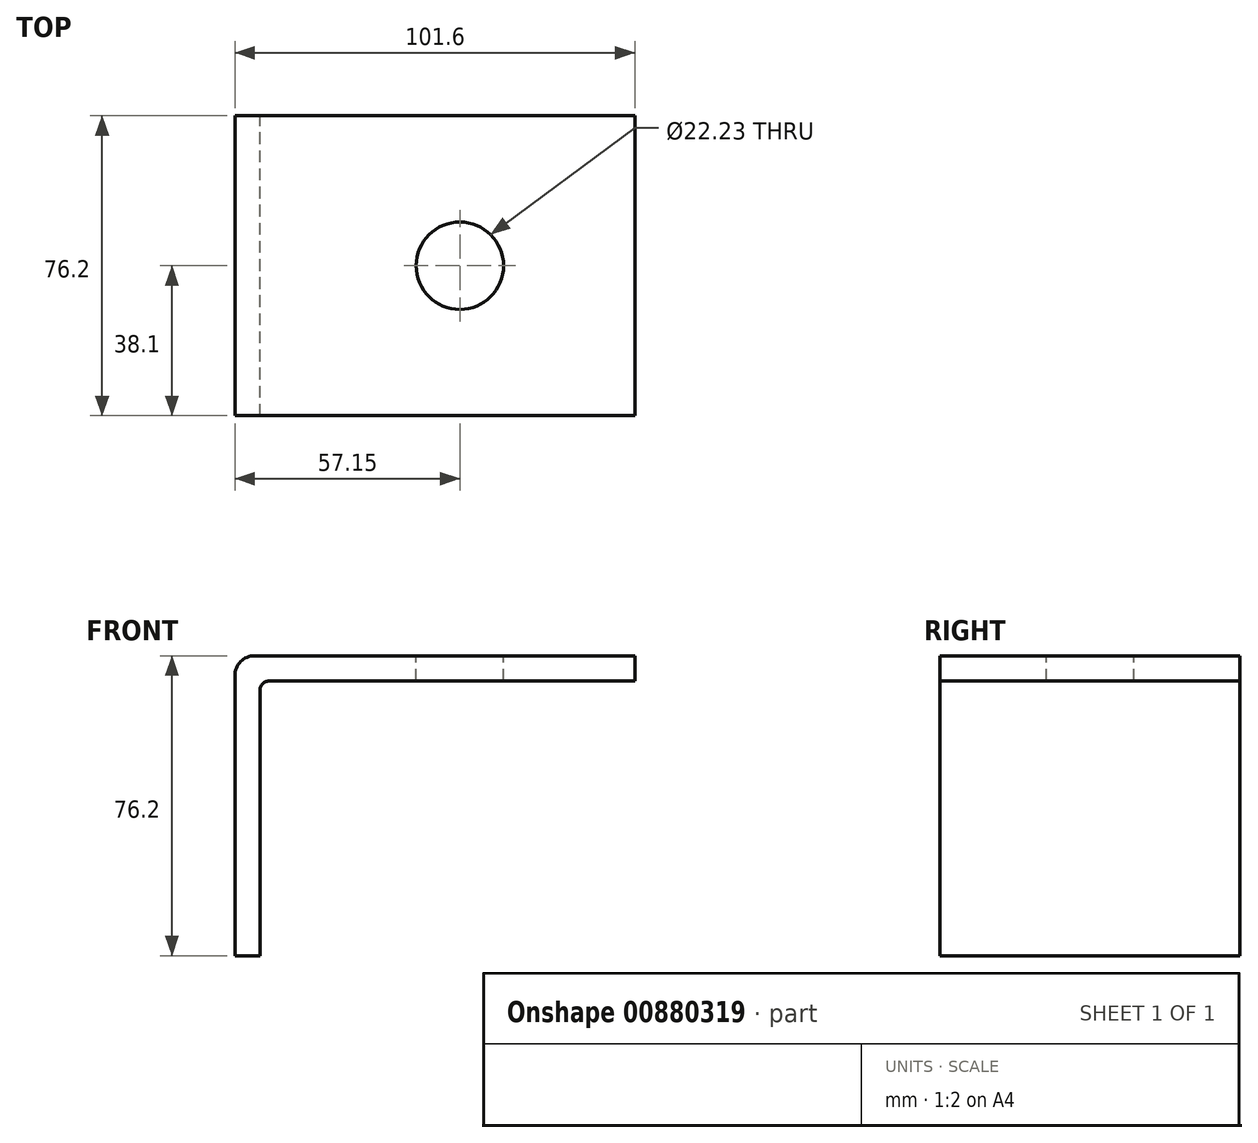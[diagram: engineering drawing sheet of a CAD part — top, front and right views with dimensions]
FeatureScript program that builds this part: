
annotation { "Feature Type Name" : "Feature", "Feature Type Description" : "" }
export const myFeature = defineFeature(function(context is Context, id is Id, definition is map)
    precondition{}
    {
        {
            var Q0;
            Q0=qCreatedBy(makeId("Front.planeOp"),FACE);
            var sketch = newSketch(context, id + "F0", { "sketchPlane" : qUnion([Q0])});
            skLineSegment(sketch, "E0", {"start": v(0, 0) * mm, "end": v(-6.35, 0) * mm});
            skLineSegment(sketch, "E1", {"start": v(-6.35, 0) * mm, "end": v(-6.35, 76.2) * mm});
            skLineSegment(sketch, "E2", {"start": v(-6.35, 76.2) * mm, "end": v(95.25, 76.2) * mm});
            skLineSegment(sketch, "E3", {"start": v(95.25, 76.2) * mm, "end": v(95.25, 69.85) * mm});
            skLineSegment(sketch, "E4", {"start": v(95.25, 69.85) * mm, "end": v(0, 69.85) * mm});
            skLineSegment(sketch, "E5", {"start": v(0, 69.85) * mm, "end": v(0, 0) * mm});
            skSolve(sketch);
        }
        {
            var Q0;
            Q0=makeQuery(id+"F0.imprint","IMPRINT",FACE,{"disambiguationData":[TD([[makeQuery(id+"F0.imprint","IMPRINT",EDGE,{"derivedFrom":sQuery(id+"F0.wireOp",EDGE,"E0")}),-1.0]])]});
            extrude(context, id + "F1", {"entities" : qUnion([Q0]), "depth" : 38.1 * mm, "offsetDistance" : 25.4 * mm, "hasSecondDirection" : true, "secondDirectionOppositeDirection" : true, "secondDirectionDepth" : 38.1 * mm});
        }
        {
            var Q0;
            Q0=makeQuery(id+"F1.opExtrude","SWEPT_EDGE",EDGE,{"disambiguationData":[OSD([sQuery(id+"F0.wireOp",EDGE,"E1"),sQuery(id+"F0.wireOp",EDGE,"E2")])]});
            fillet(context, id + "F2", {"entities" : qUnion([Q0]), "radius" : 5.08 * mm, "tangentPropagation" : true, "allowEdgeOverflow" : false});
        }
        {
            var Q0;
            Q0=makeQuery(id+"F1.opExtrude","SWEPT_EDGE",EDGE,{"disambiguationData":[OSD([sQuery(id+"F0.wireOp",EDGE,"E4"),sQuery(id+"F0.wireOp",EDGE,"E5")])]});
            fillet(context, id + "F3", {"entities" : qUnion([Q0]), "radius" : 2.54 * mm, "tangentPropagation" : true, "allowEdgeOverflow" : false});
        }
        {
            var Q0;
            Q0=makeQuery(id+"F1.opExtrude","SWEPT_FACE",FACE,{"disambiguationData":[OSD([sQuery(id+"F0.wireOp",EDGE,"E2")])]});
            var sketch = newSketch(context, id + "F4", { "sketchPlane" : qUnion([Q0])});
            skCircle(sketch, "E6", {"center": v(50.8, 0) * mm, "radius": 11.11 * mm});
            skPoint(sketch, "E6.centerSnap0", {"position": v(95.25, 0) * mm});
            skSolve(sketch);
        }
        {
            var Q0;
            Q0=makeQuery(id+"F4.imprint","IMPRINT",FACE,{"disambiguationData":[TD([[makeQuery(id+"F4.imprint","IMPRINT",EDGE,{"derivedFrom":sQuery(id+"F4.wireOp",EDGE,"E6")}),1.0]])]});
            extrude(context, id + "F5", {"entities" : qUnion([Q0]), "operationType" : NewBodyOperationType.REMOVE, "oppositeDirection" : true, "depth" : 25.4 * mm, "offsetDistance" : 25.4 * mm});
        }
    });
